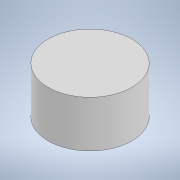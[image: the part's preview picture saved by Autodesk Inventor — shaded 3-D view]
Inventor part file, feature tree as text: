
AUTODESK INVENTOR PART (.ipt)
format: ipt  version: 2021 (Build 250183000, 183)  size: 88,064 bytes
history: native  units: mm
features: extrude x1, sketch x1
ambient origin geometry x8: Origin, YZ Plane, XZ Plane, XY Plane, X Axis, Y Axis, Z Axis, Center Point
bodies: Solid1 (feature_tree)
feature tree (2):
  extrude  "Extrusion1"  Depth=50.0mm TaperAngle=0.0deg
  sketch  "Sketch1"  dims[d0=90.0mm d1=50.0mm d2=0.0mm]
